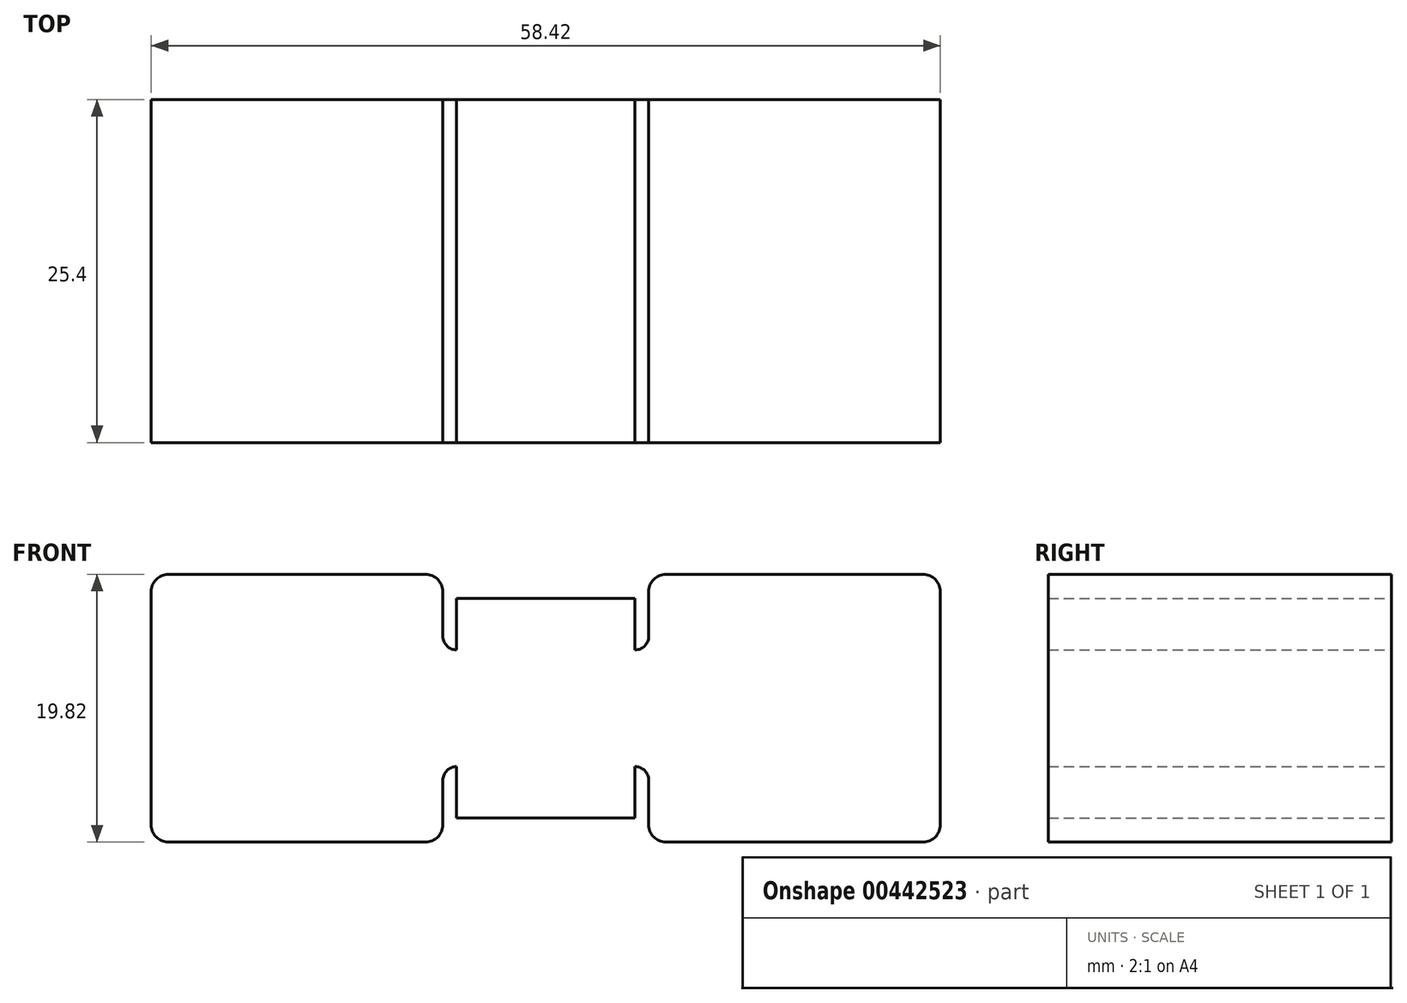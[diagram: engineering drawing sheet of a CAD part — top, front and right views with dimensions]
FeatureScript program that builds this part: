
annotation { "Feature Type Name" : "Feature", "Feature Type Description" : "" }
export const myFeature = defineFeature(function(context is Context, id is Id, definition is map)
    precondition{}
    {
        {
            var Q0;
            Q0=qCreatedBy(makeId("Front.planeOp"),FACE);
            var sketch = newSketch(context, id + "F0", { "sketchPlane" : qUnion([Q0])});
            skLineSegment(sketch, "E0", {"start": v(-29.21, 0) * mm, "end": v(-29.21, 8.64) * mm});
            skLineSegment(sketch, "E1", {"start": v(-27.94, 9.9) * mm, "end": v(-8.9, 9.9) * mm});
            skLineSegment(sketch, "E2", {"start": v(-7.62, 8.64) * mm, "end": v(-7.62, 5.33) * mm});
            skLineSegment(sketch, "E3", {"start": v(-6.6, 4.32) * mm, "end": v(-6.6, 4.32) * mm});
            skLineSegment(sketch, "E4", {"start": v(-6.6, 4.32) * mm, "end": v(-6.6, 8.13) * mm});
            skLineSegment(sketch, "E5", {"start": v(-6.6, 8.13) * mm, "end": v(0, 8.13) * mm});
            skPoint(sketch, "E6.visualSharp", {"position": v(-7.62, 4.32) * mm});
            skArc(sketch, "E6.filletArc", {"start": v(-7.62, 5.33) * mm, "mid": v(-7.32, 4.62) * mm, "end": v(-6.6, 4.32) * mm});
            skPoint(sketch, "E7.visualSharp", {"position": v(-7.62, 9.9) * mm});
            skArc(sketch, "E7.filletArc", {"start": v(-7.62, 8.64) * mm, "mid": v(-8, 9.53) * mm, "end": v(-8.9, 9.9) * mm});
            skPoint(sketch, "E8.visualSharp", {"position": v(-29.21, 9.9) * mm});
            skArc(sketch, "E8.filletArc", {"start": v(-27.94, 9.9) * mm, "mid": v(-28.84, 9.53) * mm, "end": v(-29.21, 8.64) * mm});
            skArc(sketch, "E9.MirrorCS", {"start": v(7.62, 5.33) * mm, "mid": v(7.32, 4.62) * mm, "end": v(6.6, 4.32) * mm});
            skArc(sketch, "E10.MirrorCS", {"start": v(7.62, 8.64) * mm, "mid": v(8, 9.53) * mm, "end": v(8.9, 9.9) * mm});
            skArc(sketch, "E11.MirrorCS", {"start": v(27.94, 9.9) * mm, "mid": v(28.84, 9.53) * mm, "end": v(29.21, 8.64) * mm});
            skPoint(sketch, "E12.MirrorP", {"position": v(7.62, 4.32) * mm});
            skLineSegment(sketch, "E13.MirrorCS", {"start": v(6.6, 4.32) * mm, "end": v(6.6, 8.13) * mm});
            skLineSegment(sketch, "E14.MirrorCS", {"start": v(6.6, 8.13) * mm, "end": v(0, 8.13) * mm});
            skLineSegment(sketch, "E15.MirrorCS", {"start": v(27.94, 9.9) * mm, "end": v(8.9, 9.9) * mm});
            skPoint(sketch, "E16.MirrorP", {"position": v(29.21, 9.9) * mm});
            skLineSegment(sketch, "E17.MirrorCS", {"start": v(7.62, 8.64) * mm, "end": v(7.62, 5.33) * mm});
            skLineSegment(sketch, "E18.MirrorCS", {"start": v(29.21, 0) * mm, "end": v(29.21, 8.64) * mm});
            skLineSegment(sketch, "E19.MirrorCS", {"start": v(6.6, 4.32) * mm, "end": v(6.6, 4.32) * mm});
            skPoint(sketch, "E20.MirrorP", {"position": v(7.62, 9.9) * mm});
            skArc(sketch, "E21.MirrorCS", {"start": v(-7.62, -5.33) * mm, "mid": v(-7.32, -4.62) * mm, "end": v(-6.6, -4.32) * mm});
            skArc(sketch, "E22.MirrorCS", {"start": v(7.62, -5.33) * mm, "mid": v(7.32, -4.62) * mm, "end": v(6.6, -4.32) * mm});
            skArc(sketch, "E23.MirrorCS", {"start": v(-7.62, -8.64) * mm, "mid": v(-8, -9.53) * mm, "end": v(-8.9, -9.9) * mm});
            skArc(sketch, "E24.MirrorCS", {"start": v(7.62, -8.64) * mm, "mid": v(8, -9.53) * mm, "end": v(8.9, -9.9) * mm});
            skArc(sketch, "E25.MirrorCS", {"start": v(-27.94, -9.9) * mm, "mid": v(-28.84, -9.53) * mm, "end": v(-29.21, -8.64) * mm});
            skArc(sketch, "E26.MirrorCS", {"start": v(27.94, -9.9) * mm, "mid": v(28.84, -9.53) * mm, "end": v(29.21, -8.64) * mm});
            skPoint(sketch, "E27.MirrorP", {"position": v(-29.21, -9.9) * mm});
            skLineSegment(sketch, "E28.MirrorCS", {"start": v(6.6, -8.13) * mm, "end": v(0, -8.13) * mm});
            skPoint(sketch, "E29.MirrorP", {"position": v(7.62, -4.32) * mm});
            skPoint(sketch, "E30.MirrorP", {"position": v(7.62, -9.9) * mm});
            skLineSegment(sketch, "E31.MirrorCS", {"start": v(-6.6, -4.32) * mm, "end": v(-6.6, -8.13) * mm});
            skLineSegment(sketch, "E32.MirrorCS", {"start": v(-6.6, -8.13) * mm, "end": v(0, -8.13) * mm});
            skLineSegment(sketch, "E33.MirrorCS", {"start": v(-6.6, -4.32) * mm, "end": v(-6.6, -4.32) * mm});
            skLineSegment(sketch, "E34.MirrorCS", {"start": v(29.21, 0) * mm, "end": v(29.21, -8.64) * mm});
            skLineSegment(sketch, "E35.MirrorCS", {"start": v(-27.94, -9.9) * mm, "end": v(-8.9, -9.9) * mm});
            skLineSegment(sketch, "E36.MirrorCS", {"start": v(6.6, -4.32) * mm, "end": v(6.6, -4.32) * mm});
            skLineSegment(sketch, "E37.MirrorCS", {"start": v(-29.21, 0) * mm, "end": v(-29.21, -8.64) * mm});
            skLineSegment(sketch, "E38.MirrorCS", {"start": v(-7.62, -8.64) * mm, "end": v(-7.62, -5.33) * mm});
            skLineSegment(sketch, "E39.MirrorCS", {"start": v(6.6, -4.32) * mm, "end": v(6.6, -8.13) * mm});
            skLineSegment(sketch, "E40.MirrorCS", {"start": v(7.62, -8.64) * mm, "end": v(7.62, -5.33) * mm});
            skLineSegment(sketch, "E41.MirrorCS", {"start": v(27.94, -9.9) * mm, "end": v(8.9, -9.9) * mm});
            skPoint(sketch, "E42.MirrorP", {"position": v(29.21, -9.9) * mm});
            skPoint(sketch, "E43.MirrorP", {"position": v(-7.62, -4.32) * mm});
            skPoint(sketch, "E44.MirrorP", {"position": v(-7.62, -9.9) * mm});
            skSolve(sketch);
        }
        {
            var Q0;
            Q0=makeQuery(id+"F0.imprint","IMPRINT",FACE,{"disambiguationData":[TD([[makeQuery(id+"F0.imprint","IMPRINT",EDGE,{"derivedFrom":sQuery(id+"F0.wireOp",EDGE,"E0")}),-1.0]])]});
            extrude(context, id + "F1", {"entities" : qUnion([Q0]), "depth" : 25.4 * mm});
        }
    });
